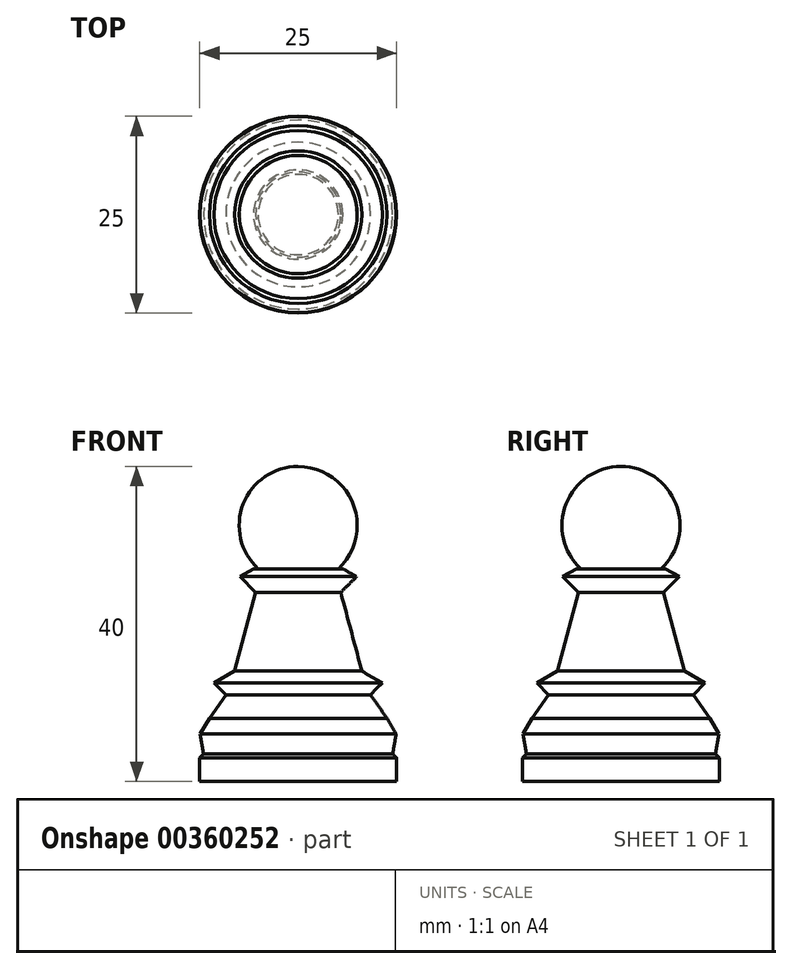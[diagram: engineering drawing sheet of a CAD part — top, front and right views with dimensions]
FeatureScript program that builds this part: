
annotation { "Feature Type Name" : "Feature", "Feature Type Description" : "" }
export const myFeature = defineFeature(function(context is Context, id is Id, definition is map)
    precondition{}
    {
        {
            var Q0;
            Q0=qCreatedBy(makeId("Top.planeOp"),FACE);
            var sketch = newSketch(context, id + "F0", { "sketchPlane" : qUnion([Q0])});
            skCircle(sketch, "E0", {"center": v(0, 0) * mm, "radius": 12.5 * mm});
            skSolve(sketch);
        }
        {
            var Q0;
            Q0=makeQuery(id+"F0.imprint","IMPRINT",FACE,{"disambiguationData":[TD([[makeQuery(id+"F0.imprint","IMPRINT",EDGE,{"derivedFrom":sQuery(id+"F0.wireOp",EDGE,"E0")}),1.0]])]});
            var Q1;
            Q1=sQuery(id+"F0.wireOp",EDGE,"E0");
            extrude(context, id + "F1", {"entities" : qUnion([Q0]), "surfaceEntities" : qUnion([Q1]), "depth" : 3 * mm});
        }
        {
            var Q0;
            Q0=makeQuery(id+"F1.opExtrude","CAP_FACE",FACE,{"disambiguationData":[OSD([sQuery(id+"F0.wireOp",EDGE,"E0")])],"isStart":false});
            extrude(context, id + "F2", {"entities" : qUnion([Q0]), "operationType" : NewBodyOperationType.ADD, "depth" : 0.5 * mm, "hasDraft" : true, "draftAngle" : 45 * degree, "draftPullDirection" : true});
        }
        {
            var Q0;
            Q0=makeQuery(id+"F2.opExtrude","CAP_FACE",FACE,{"disambiguationData":[OSD([sQuery(id+"F0.wireOp",EDGE,"E0")])],"isStart":false});
            extrude(context, id + "F3", {"entities" : qUnion([Q0]), "operationType" : NewBodyOperationType.ADD, "depth" : 2.5 * mm, "hasDraft" : true, "draftAngle" : 10 * degree});
        }
        {
            var Q0;
            Q0=makeQuery(id+"F3.opExtrude","CAP_FACE",FACE,{"disambiguationData":[OSD([sQuery(id+"F0.wireOp",EDGE,"E0")])],"isStart":false});
            extrude(context, id + "F4", {"entities" : qUnion([Q0]), "operationType" : NewBodyOperationType.ADD, "depth" : 2 * mm, "hasDraft" : true, "draftAngle" : 30 * degree, "draftPullDirection" : true});
        }
        {
            var Q0;
            Q0=makeQuery(id+"F4.opExtrude","CAP_FACE",FACE,{"disambiguationData":[OSD([sQuery(id+"F0.wireOp",EDGE,"E0")])],"isStart":false});
            extrude(context, id + "F5", {"entities" : qUnion([Q0]), "operationType" : NewBodyOperationType.ADD, "depth" : 3 * mm, "hasDraft" : true, "draftAngle" : 35 * degree, "draftPullDirection" : true});
        }
        {
            var Q0;
            Q0=makeQuery(id+"F5.opExtrude","CAP_FACE",FACE,{"disambiguationData":[OSD([sQuery(id+"F0.wireOp",EDGE,"E0")])],"isStart":false});
            extrude(context, id + "F6", {"entities" : qUnion([Q0]), "operationType" : NewBodyOperationType.ADD, "depth" : 1.5 * mm, "hasDraft" : true, "draftAngle" : 45 * degree});
        }
        {
            var Q0;
            Q0=makeQuery(id+"F6.opExtrude","CAP_FACE",FACE,{"disambiguationData":[OSD([sQuery(id+"F0.wireOp",EDGE,"E0")])],"isStart":false});
            extrude(context, id + "F7", {"entities" : qUnion([Q0]), "operationType" : NewBodyOperationType.ADD, "depth" : 1.5 * mm, "hasDraft" : true, "draftAngle" : 60 * degree, "draftPullDirection" : true});
        }
        {
            var Q0;
            Q0=makeQuery(id+"F7.opExtrude","CAP_FACE",FACE,{"disambiguationData":[OSD([sQuery(id+"F0.wireOp",EDGE,"E0")])],"isStart":false});
            extrude(context, id + "F8", {"entities" : qUnion([Q0]), "operationType" : NewBodyOperationType.ADD, "depth" : 10 * mm, "hasDraft" : true, "draftAngle" : 15 * degree, "draftPullDirection" : true});
        }
        {
            var Q0;
            Q0=makeQuery(id+"F8.opExtrude","CAP_FACE",FACE,{"disambiguationData":[OSD([sQuery(id+"F0.wireOp",EDGE,"E0")])],"isStart":false});
            extrude(context, id + "F9", {"entities" : qUnion([Q0]), "operationType" : NewBodyOperationType.ADD, "depth" : 2 * mm, "hasDraft" : true, "draftAngle" : 45 * degree});
        }
        {
            var Q0;
            Q0=makeQuery(id+"F9.opExtrude","CAP_FACE",FACE,{"disambiguationData":[OSD([sQuery(id+"F0.wireOp",EDGE,"E0")])],"isStart":false});
            extrude(context, id + "F10", {"entities" : qUnion([Q0]), "operationType" : NewBodyOperationType.ADD, "depth" : 1 * mm, "hasDraft" : true, "draftAngle" : 60 * degree, "draftPullDirection" : true});
        }
        {
            var Q0;
            Q0=qCreatedBy(makeId("Front.planeOp"),FACE);
            var sketch = newSketch(context, id + "F11", { "sketchPlane" : qUnion([Q0])});
            skLineSegment(sketch, "E1", {"start": v(0, 0) * mm, "end": v(0, 32.5) * mm});
            skCircle(sketch, "E2", {"center": v(0, 32.5) * mm, "radius": 7.5 * mm});
            skLineSegment(sketch, "E3", {"start": v(0, 32.5) * mm, "end": v(0, 45.92) * mm});
            skSolve(sketch);
        }
        {
            var Q0;
            {var subQ0=sQuery(id+"F11.wireOp",EDGE,"E3");var subQ1=sQuery(id+"F11.wireOp",EDGE,"E1");var subQ2=makeQuery(id+"F11.imprint","INTERSECT",VERTEX,{"derivedFrom":[subQ1,subQ0]});Q0=makeQuery(id+"F11.imprint","IMPRINT",FACE,{"disambiguationData":[TD([[makeQuery(id+"F11.imprint","IMPRINT",EDGE,{"disambiguationData":[TD([[subQ2,1.0]])],"derivedFrom":subQ1}),1.0]])]});}
            var Q1;
            Q1=sQuery(id+"F11.wireOp",EDGE,"E1");
            revolve(context, id + "F12", {"operationType" : NewBodyOperationType.ADD, "entities" : qUnion([Q0]), "axis" : qUnion([Q1]), "revolveType" : RevolveType.FULL});
        }
    });
